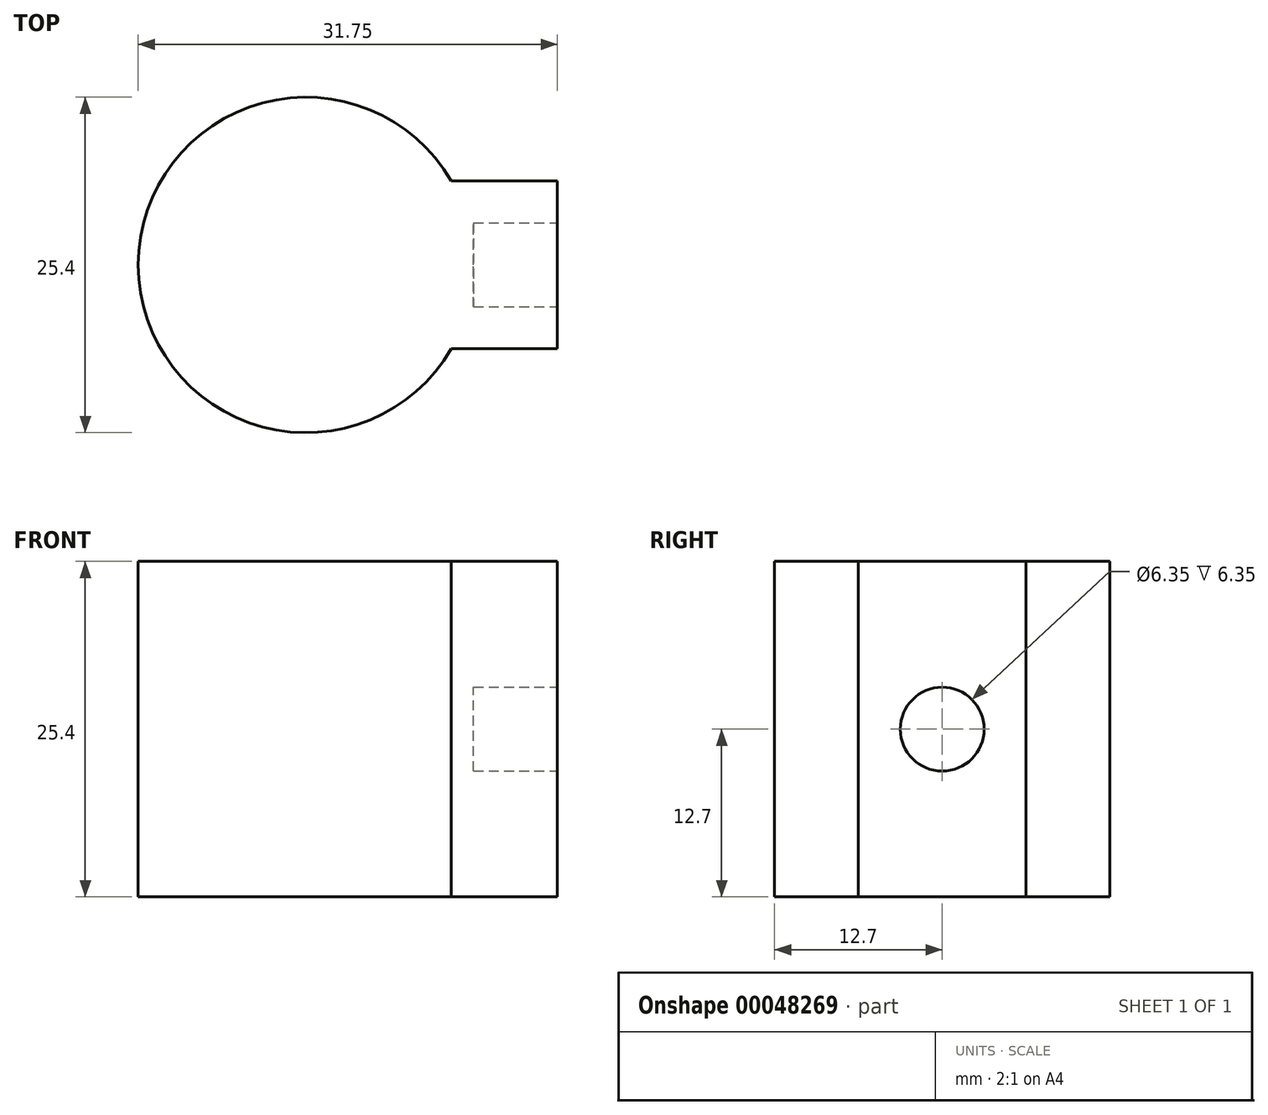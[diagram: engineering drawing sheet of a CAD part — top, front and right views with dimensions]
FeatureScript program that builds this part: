
annotation { "Feature Type Name" : "Feature", "Feature Type Description" : "" }
export const myFeature = defineFeature(function(context is Context, id is Id, definition is map)
    precondition{}
    {
        {
            var Q0;
            Q0=qCreatedBy(makeId("Top.planeOp"),FACE);
            var sketch = newSketch(context, id + "F0", { "sketchPlane" : qUnion([Q0])});
            skArc(sketch, "E0", {"start": v(11, 6.35) * mm, "mid": v(-12.7, 0) * mm, "end": v(11, -6.35) * mm});
            skLineSegment(sketch, "E1", {"start": v(11, 6.35) * mm, "end": v(19.05, 6.35) * mm});
            skLineSegment(sketch, "E2", {"start": v(19.05, 6.35) * mm, "end": v(19.05, -6.35) * mm});
            skLineSegment(sketch, "E3", {"start": v(19.05, -6.35) * mm, "end": v(11, -6.35) * mm});
            skSolve(sketch);
        }
        {
            var Q0;
            Q0 = qSketchRegion(id + "F0", true);
            extrude(context, id + "F1", {"entities" : qUnion([Q0]), "depth" : 25.4 * mm});
        }
        {
            var Q0;
            Q0=makeQuery(id+"F1.opExtrude","SWEPT_FACE",FACE,{"disambiguationData":[OSD([sQuery(id+"F0.wireOp",EDGE,"E2")])]});
            var sketch = newSketch(context, id + "F2", { "sketchPlane" : qUnion([Q0])});
            skCircle(sketch, "E4", {"center": v(0, 12.7) * mm, "radius": 3.17 * mm});
            skSolve(sketch);
        }
        {
            var Q0;
            Q0=makeQuery(id+"F2.imprint","IMPRINT",FACE,{"disambiguationData":[TD([[makeQuery(id+"F2.imprint","IMPRINT",EDGE,{"derivedFrom":sQuery(id+"F2.wireOp",EDGE,"E4")}),1.0]])]});
            extrude(context, id + "F3", {"entities" : qUnion([Q0]), "operationType" : NewBodyOperationType.REMOVE, "oppositeDirection" : true, "depth" : 6.35 * mm});
        }
    });
